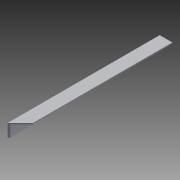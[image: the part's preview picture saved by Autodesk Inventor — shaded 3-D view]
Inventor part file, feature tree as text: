
AUTODESK INVENTOR PART (.ipt)
format: ipt  version: 2014 (Build 180170000, 170)  size: 81,920 bytes
history: native  units: in
note: dims shown in document units (in); Inventor stores cm internally (conversion verified against a paired STEP export)
features: extrude x2, sketch x2
ambient origin geometry x8: Origin, YZ Plane, XZ Plane, XY Plane, X Axis, Y Axis, Z Axis, Center Point
bodies: Solid1 (feature_tree)
feature tree (4):
  extrude  "Extrusion1"  Depth=0.5in
  extrude  "Extrusion3"  Depth=0.45in
  sketch  "Sketch1"  dims[d0=0.5in d1=0.5in]
  sketch  "Sketch3"  dims[d2=0.05in d3=0.45in d4=6.0in d5=0.0in d10=45.0deg d11=1.0in d12=0.0in]
